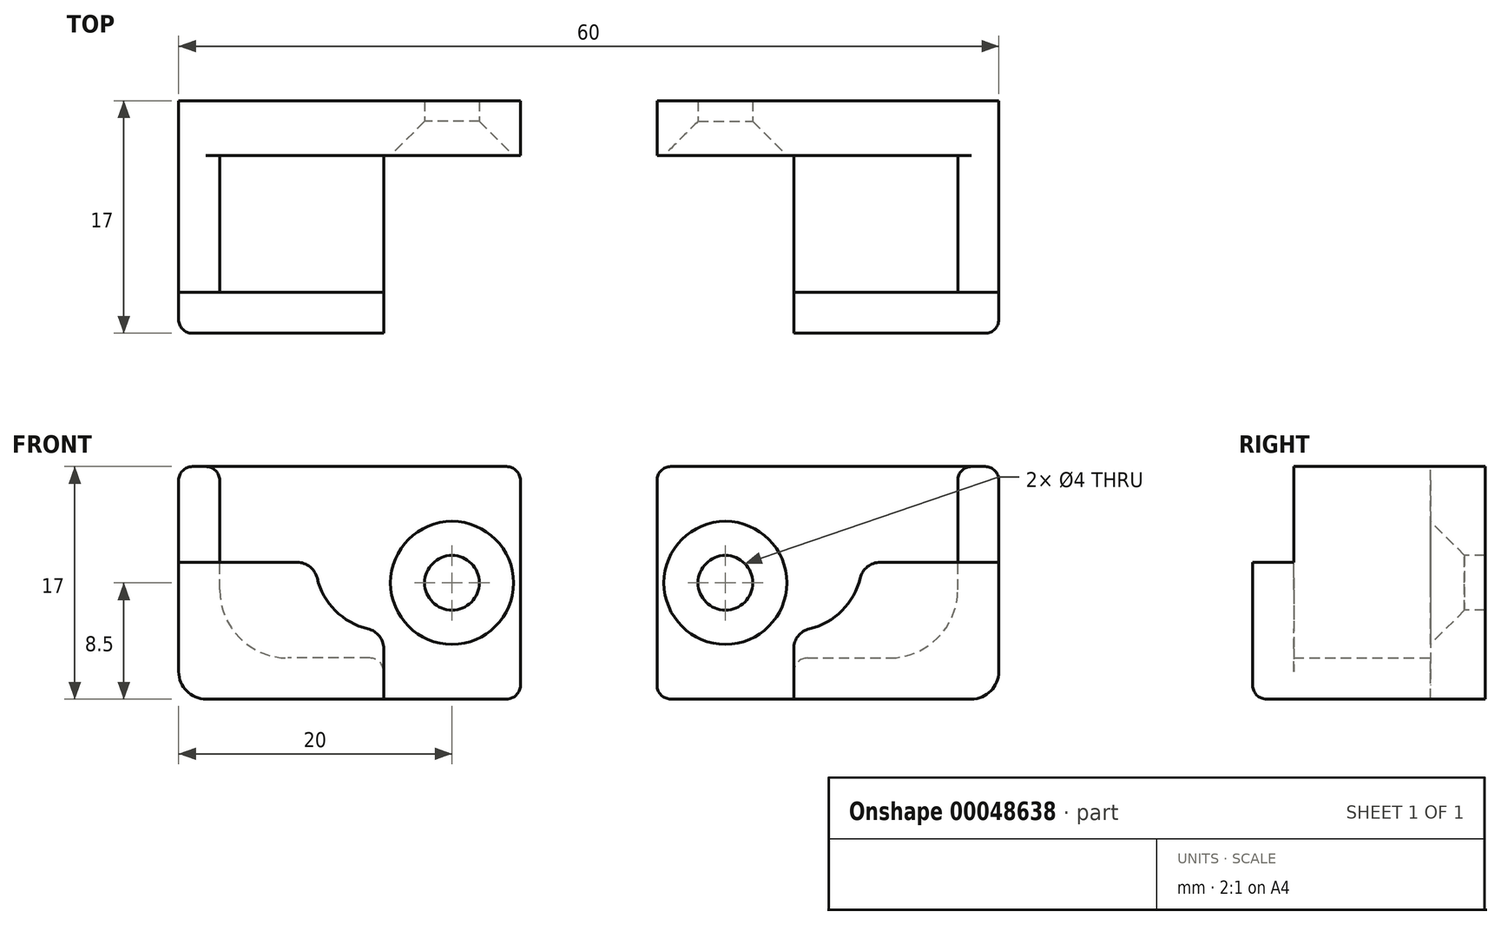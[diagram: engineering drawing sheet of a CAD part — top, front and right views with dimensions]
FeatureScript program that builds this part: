
annotation { "Feature Type Name" : "Feature", "Feature Type Description" : "" }
export const myFeature = defineFeature(function(context is Context, id is Id, definition is map)
    precondition{}
    {
        {
            var Q0;
            Q0=qCreatedBy(makeId("Top.planeOp"),FACE);
            var sketch = newSketch(context, id + "F0", { "sketchPlane" : qUnion([Q0])});
            skLineSegment(sketch, "E0.bottom", {"start": v(-25, 17) * mm, "end": v(0, 17) * mm});
            skLineSegment(sketch, "E0.top", {"start": v(-25, 0) * mm, "end": v(0, 0) * mm});
            skLineSegment(sketch, "E0.left", {"start": v(-25, 17) * mm, "end": v(-25, 0) * mm});
            skLineSegment(sketch, "E0.right", {"start": v(0, 17) * mm, "end": v(0, 0) * mm});
            skSolve(sketch);
        }
        {
            var Q0;
            Q0=makeQuery(id+"F0.imprint","IMPRINT",FACE,{"disambiguationData":[TD([[makeQuery(id+"F0.imprint","IMPRINT",EDGE,{"derivedFrom":sQuery(id+"F0.wireOp",EDGE,"E0.bottom")}),-1.0]])]});
            extrude(context, id + "F1", {"entities" : qUnion([Q0]), "depth" : 4 * mm});
        }
        {
            var Q0;
            Q0=makeQuery(id+"F1.opExtrude","CAP_FACE",FACE,{"disambiguationData":[OSD([sQuery(id+"F0.wireOp",EDGE,"E0.bottom"),sQuery(id+"F0.wireOp",EDGE,"E0.top"),sQuery(id+"F0.wireOp",EDGE,"E0.left"),sQuery(id+"F0.wireOp",EDGE,"E0.right")])],"isStart":false});
            var sketch = newSketch(context, id + "F2", { "sketchPlane" : qUnion([Q0])});
            skLineSegment(sketch, "E1", {"start": v(-25, 17) * mm, "end": v(-25, 0) * mm});
            skLineSegment(sketch, "E2", {"start": v(-25, 0) * mm, "end": v(-10, 0) * mm});
            skLineSegment(sketch, "E3", {"start": v(-10, 0) * mm, "end": v(-10, 3) * mm});
            skLineSegment(sketch, "E4", {"start": v(-10, 3) * mm, "end": v(-22, 3) * mm});
            skLineSegment(sketch, "E5", {"start": v(-22, 3) * mm, "end": v(-22, 17) * mm});
            skLineSegment(sketch, "E6", {"start": v(-22, 17) * mm, "end": v(-25, 17) * mm});
            skSolve(sketch);
        }
        {
            var Q0;
            Q0=makeQuery(id+"F2.imprint","IMPRINT",FACE,{"disambiguationData":[TD([[makeQuery(id+"F2.imprint","IMPRINT",EDGE,{"derivedFrom":sQuery(id+"F2.wireOp",EDGE,"E1")}),1.0]])]});
            extrude(context, id + "F3", {"entities" : qUnion([Q0]), "operationType" : NewBodyOperationType.ADD, "depth" : 10 * mm});
        }
        {
            var Q0;
            Q0=makeQuery(id+"F1.opExtrude","CAP_FACE",FACE,{"disambiguationData":[OSD([sQuery(id+"F0.wireOp",EDGE,"E0.bottom"),sQuery(id+"F0.wireOp",EDGE,"E0.top"),sQuery(id+"F0.wireOp",EDGE,"E0.left"),sQuery(id+"F0.wireOp",EDGE,"E0.right")])],"isStart":false});
            var sketch = newSketch(context, id + "F4", { "sketchPlane" : qUnion([Q0])});
            skPoint(sketch, "E7", {"position": v(-5, 8.5) * mm});
            skPoint(sketch, "E7.positionSnap0", {"position": v(0, 8.5) * mm});
            skLineSegment(sketch, "E8", {"start": v(-5, 0) * mm, "end": v(-5, 17) * mm, "construction": true});
            skSolve(sketch);
        }
        {
            var Q0;
            Q0=sQuery(id+"F4.wireOp",VERTEX,"E7");
            var Q1;
            Q1=makeQuery(id+"F1.opExtrude","SWEPT_BODY",BODY,{"disambiguationData":[OSD([sQuery(id+"F0.wireOp",EDGE,"E0.bottom"),sQuery(id+"F0.wireOp",EDGE,"E0.top"),sQuery(id+"F0.wireOp",EDGE,"E0.left"),sQuery(id+"F0.wireOp",EDGE,"E0.right")])]});
            hole(context, id + "F5", {"style" : HoleStyle.C_SINK, "holeDiameter" : 4 * mm, "cSinkDiameter" : 9 * mm, "endStyle" : HoleEndStyle.THROUGH, "locations" : qUnion([Q0]), "scope" : qUnion([Q1]), "cSinkAngle" : 90 * degree});
        }
        {
            var Q0;
            Q0=makeQuery(id+"F3.opExtrude","CAP_FACE",FACE,{"disambiguationData":[OSD([sQuery(id+"F2.wireOp",EDGE,"E1"),sQuery(id+"F2.wireOp",EDGE,"E2"),sQuery(id+"F2.wireOp",EDGE,"E3"),sQuery(id+"F2.wireOp",EDGE,"E4"),sQuery(id+"F2.wireOp",EDGE,"E5"),sQuery(id+"F2.wireOp",EDGE,"E6")])],"isStart":false});
            var sketch = newSketch(context, id + "F6", { "sketchPlane" : qUnion([Q0])});
            skLineSegment(sketch, "E9.bottom", {"start": v(-25, 10) * mm, "end": v(-16.32, 10) * mm});
            skLineSegment(sketch, "E9.top", {"start": v(-25, 0) * mm, "end": v(-10, 0) * mm});
            skLineSegment(sketch, "E9.left", {"start": v(-25, 10) * mm, "end": v(-25, 0) * mm});
            skLineSegment(sketch, "E9.right", {"start": v(-10, 10) * mm, "end": v(-10, 5) * mm, "construction": true});
            skArc(sketch, "E10", {"start": v(-14.87, 8.85) * mm, "mid": v(-13.54, 6.46) * mm, "end": v(-11.15, 5.13) * mm});
            skLineSegment(sketch, "E11", {"start": v(-15, 10) * mm, "end": v(-10, 10) * mm, "construction": true});
            skLineSegment(sketch, "E12", {"start": v(-10, 3.68) * mm, "end": v(-10, 0) * mm});
            skPoint(sketch, "E13.visualSharp", {"position": v(-15, 10) * mm});
            skArc(sketch, "E13.filletArc", {"start": v(-14.87, 8.85) * mm, "mid": v(-15.4, 9.68) * mm, "end": v(-16.32, 10) * mm});
            skPoint(sketch, "E14.visualSharp", {"position": v(-10, 5) * mm});
            skArc(sketch, "E14.filletArc", {"start": v(-10, 3.68) * mm, "mid": v(-10.32, 4.6) * mm, "end": v(-11.15, 5.13) * mm});
            skSolve(sketch);
        }
        {
            var Q0;
            {var subQ1=makeQuery(id+"F3.opExtrude","CAP_EDGE",EDGE,{"disambiguationData":[OSD([sQuery(id+"F2.wireOp",EDGE,"E4")])],"isStart":false});Q0=makeQuery(id+"F6.imprint","IMPRINT",FACE,{"disambiguationData":[TD([[makeQuery(id+"F6.imprint","IMPRINT",EDGE,{"derivedFrom":subQ1}),-1.0]])]});}
            var Q1;
            {var subQ4=sQuery(id+"F6.wireOp",EDGE,"E9.top");Q1=makeQuery(id+"F6.imprint","IMPRINT",FACE,{"disambiguationData":[TD([[makeQuery(id+"F6.imprint","IMPRINT",EDGE,{"derivedFrom":subQ4}),1.0]])]});}
            extrude(context, id + "F7", {"entities" : qUnion([Q0, Q1]), "operationType" : NewBodyOperationType.ADD, "depth" : 3 * mm});
        }
        {
            var Q0;
            Q0=makeQuery(id+"F3.opExtrude","SWEPT_EDGE",EDGE,{"disambiguationData":[OSD([sQuery(id+"F2.wireOp",EDGE,"E4"),sQuery(id+"F2.wireOp",EDGE,"E5")])]});
            fillet(context, id + "F8", {"entities" : qUnion([Q0]), "radius" : 5 * mm, "tangentPropagation" : true, "allowEdgeOverflow" : false});
        }
        {
            var Q0;
            Q0=makeQuery(id+"F1.opExtrude","SWEPT_BODY",BODY,{"disambiguationData":[OSD([sQuery(id+"F0.wireOp",EDGE,"E0.bottom"),sQuery(id+"F0.wireOp",EDGE,"E0.top"),sQuery(id+"F0.wireOp",EDGE,"E0.left"),sQuery(id+"F0.wireOp",EDGE,"E0.right")])]});
            var Q1;
            Q1=makeQuery(id+"F1.opExtrude","CAP_EDGE",EDGE,{"disambiguationData":[OSD([sQuery(id+"F0.wireOp",EDGE,"E0.top")])],"isStart":true});
            transform(context, id + "F9", {"entities" : qUnion([Q0]), "transformType" : TransformType.ROTATION, "transformAxis" : qUnion([Q1]), "angle" : 90 * degree, "makeCopy" : false});
        }
        {
            var Q0;
            Q0=makeQuery(id+"F1.opExtrude","SWEPT_EDGE",EDGE,{"disambiguationData":[OSD([sQuery(id+"F0.wireOp",EDGE,"E0.bottom"),sQuery(id+"F0.wireOp",EDGE,"E0.right")])]});
            var Q1;
            Q1=makeQuery(id+"F1.opExtrude","SWEPT_EDGE",EDGE,{"disambiguationData":[OSD([sQuery(id+"F0.wireOp",EDGE,"E0.top"),sQuery(id+"F0.wireOp",EDGE,"E0.right")])]});
            var Q2;
            Q2=makeQuery(id+"F7.opExtrude","SWEPT_EDGE",EDGE,{"disambiguationData":[OSD([sQuery(id+"F6.wireOp",EDGE,"E9.bottom"),sQuery(id+"F6.wireOp",EDGE,"E9.right")])]});
            var Q3;
            Q3=makeQuery(id+"F3.boolean.opBoolean","MERGE",EDGE,{"derivedFrom":[makeQuery(id+"F1.opExtrude","SWEPT_EDGE",EDGE,{"disambiguationData":[OSD([sQuery(id+"F0.wireOp",EDGE,"E0.bottom"),sQuery(id+"F0.wireOp",EDGE,"E0.left")])]}),makeQuery(id+"F3.opExtrude","SWEPT_EDGE",EDGE,{"disambiguationData":[OSD([sQuery(id+"F2.wireOp",EDGE,"E1"),sQuery(id+"F2.wireOp",EDGE,"E6")])]})]});
            var Q4;
            Q4=makeQuery(id+"F3.opExtrude","SWEPT_EDGE",EDGE,{"disambiguationData":[OSD([sQuery(id+"F0.wireOp",EDGE,"E0.bottom"),sQuery(id+"F2.wireOp",EDGE,"E5"),sQuery(id+"F2.wireOp",EDGE,"E6")])]});
            var Q5;
            Q5=makeQuery(id+"F3.opExtrude","SWEPT_EDGE",EDGE,{"disambiguationData":[OSD([sQuery(id+"F2.wireOp",EDGE,"E3"),sQuery(id+"F2.wireOp",EDGE,"E4")])]});
            var Q6;
            Q6=makeQuery(id+"F7.opExtrude","CAP_EDGE",EDGE,{"disambiguationData":[OSD([sQuery(id+"F6.wireOp",EDGE,"E9.left")])],"isStart":false});
            var Q7;
            Q7=makeQuery(id+"F7.opExtrude","CAP_EDGE",EDGE,{"disambiguationData":[OSD([sQuery(id+"F6.wireOp",EDGE,"E9.top")])],"isStart":false});
            fillet(context, id + "F10", {"entities" : qUnion([Q0, Q1, Q2, Q3, Q4, Q5, Q6, Q7]), "radius" : 1 * mm, "tangentPropagation" : true, "allowEdgeOverflow" : false});
        }
        {
            var Q0;
            Q0=makeQuery(id+"F7.boolean.opBoolean","MERGE",EDGE,{"derivedFrom":[makeQuery(id+"F3.boolean.opBoolean","MERGE",EDGE,{"derivedFrom":[makeQuery(id+"F1.opExtrude","SWEPT_EDGE",EDGE,{"disambiguationData":[OSD([sQuery(id+"F0.wireOp",EDGE,"E0.top"),sQuery(id+"F0.wireOp",EDGE,"E0.left")])]}),makeQuery(id+"F3.opExtrude","SWEPT_EDGE",EDGE,{"disambiguationData":[OSD([sQuery(id+"F2.wireOp",EDGE,"E1"),sQuery(id+"F2.wireOp",EDGE,"E2")])]})]}),makeQuery(id+"F7.opExtrude","SWEPT_EDGE",EDGE,{"disambiguationData":[OSD([sQuery(id+"F6.wireOp",EDGE,"E9.top"),sQuery(id+"F6.wireOp",EDGE,"E9.left")])]})]});
            fillet(context, id + "F11", {"entities" : qUnion([Q0]), "radius" : 2 * mm, "tangentPropagation" : true, "allowEdgeOverflow" : false});
        }
        {
            var Q0;
            Q0=makeQuery(id+"F1.opExtrude","SWEPT_BODY",BODY,{"disambiguationData":[OSD([sQuery(id+"F0.wireOp",EDGE,"E0.bottom"),sQuery(id+"F0.wireOp",EDGE,"E0.top"),sQuery(id+"F0.wireOp",EDGE,"E0.left"),sQuery(id+"F0.wireOp",EDGE,"E0.right")])]});
            var Q1;
            Q1=qCreatedBy(makeId("Right.planeOp"),FACE);
            transform(context, id + "F12", {"entities" : qUnion([Q0]), "transformType" : TransformType.TRANSLATION_DISTANCE, "transformDirection" : qUnion([Q1]), "distance" : 5 * mm, "oppositeDirection" : true, "makeCopy" : false});
        }
        {
            var Q0;
            Q0=makeQuery(id+"F1.opExtrude","SWEPT_BODY",BODY,{"disambiguationData":[OSD([sQuery(id+"F0.wireOp",EDGE,"E0.bottom"),sQuery(id+"F0.wireOp",EDGE,"E0.top"),sQuery(id+"F0.wireOp",EDGE,"E0.left"),sQuery(id+"F0.wireOp",EDGE,"E0.right")])]});
            var Q1;
            Q1=qCreatedBy(makeId("Right.planeOp"),FACE);
            mirror(context, id + "F13", {"entities" : qUnion([Q0]), "mirrorPlane" : qUnion([Q1])});
        }
    });
